# Revit family: OmegaFlex-TracPipe-Manifold-4_Ports
name_source: partatom
category: Pipe Accessories
units: mm (PartAtom-declared; Revit-internal decimal feet)

## family parameters
Always vertical = Yes
Cut with Voids When Loaded = No
Part Type = Normal
Round Connector Dimension = Use Radius
Shared = No
Work Plane-Based = No

## types (3) — shared parameters
Default Elevation = 0' - 0"
Description = See Part Description
Manufacturer = OmegaFlex
Model = TracPipe CounterStrike
Nominal Diameter 3 = 1"
URL = https://www.omegaflex.com

## per-type parameters (varying)
| type | Body Inner Diameter | Body Outer Diameter | Inner Top Diameter | NPT Diameter 1 | NPT Diameter 2 | NPT Diameter 3 | Nominal Diameter 1 | Nominal Diameter 2 | Nominal Radius 1 | Nominal Radius 2 | Nominal Radius 3 | Nut Bottom Base | Socket Entrance Diameter 1 | Socket Entrance Diameter 2 | Socket Entrance Thickness | Total Heigth | TracPipe Edge Offset | TracPipe Total Length |
| 3/4" x 1/2" x 1/2" (4) | 0' - 0 31/32" | 0' - 1 3/8" | 0' - 0 29/32" | 0' - 1 1/16" | 0' - 0 27/32" | 0' - 0 27/32" | 1" | 1" | 0" | 0" | 0" | 0' - 0 13/16" | 0' - 1 7/16" | 0' - 1 5/16" | 0' - 0 9/32" | 0' - 2 1/8" | 0' - 1 5/16" | 0' - 9 9/16" |
| 1-1/4" x 1" x 3/4" (4) | 0' - 1 21/32" | 0' - 2 1/32" | 0' - 1 11/32" | 0' - 1 21/32" | 0' - 1 5/16" | 0' - 1 1/16" | 1" | 1" | 1" | 1" | 0" | 0' - 1 7/32" | 0' - 2 1/8" | 0' - 1 3/4" | 0' - 0 13/32" | 0' - 3" | 0' - 1 11/16" | 0' - 11 7/16" |
| 2" x 1-1/2" x 1" (4) | 0' - 2 23/32" | 0' - 3 1/8" | 0' - 1 19/32" | 0' - 2 3/8" | 0' - 1 29/32" | 0' - 1 5/16" | 2" | 2" | 1" | 1" | 1" | 0' - 1 7/8" | 0' - 3 1/4" | 0' - 2" | 0' - 0 19/32" | 0' - 4 3/16" | 0' - 2 5/16" | 1' - 2 9/16" |

## geometry (parser evidence)
native form markers: Sweep x4
no freeform markers — native parametric forms only
